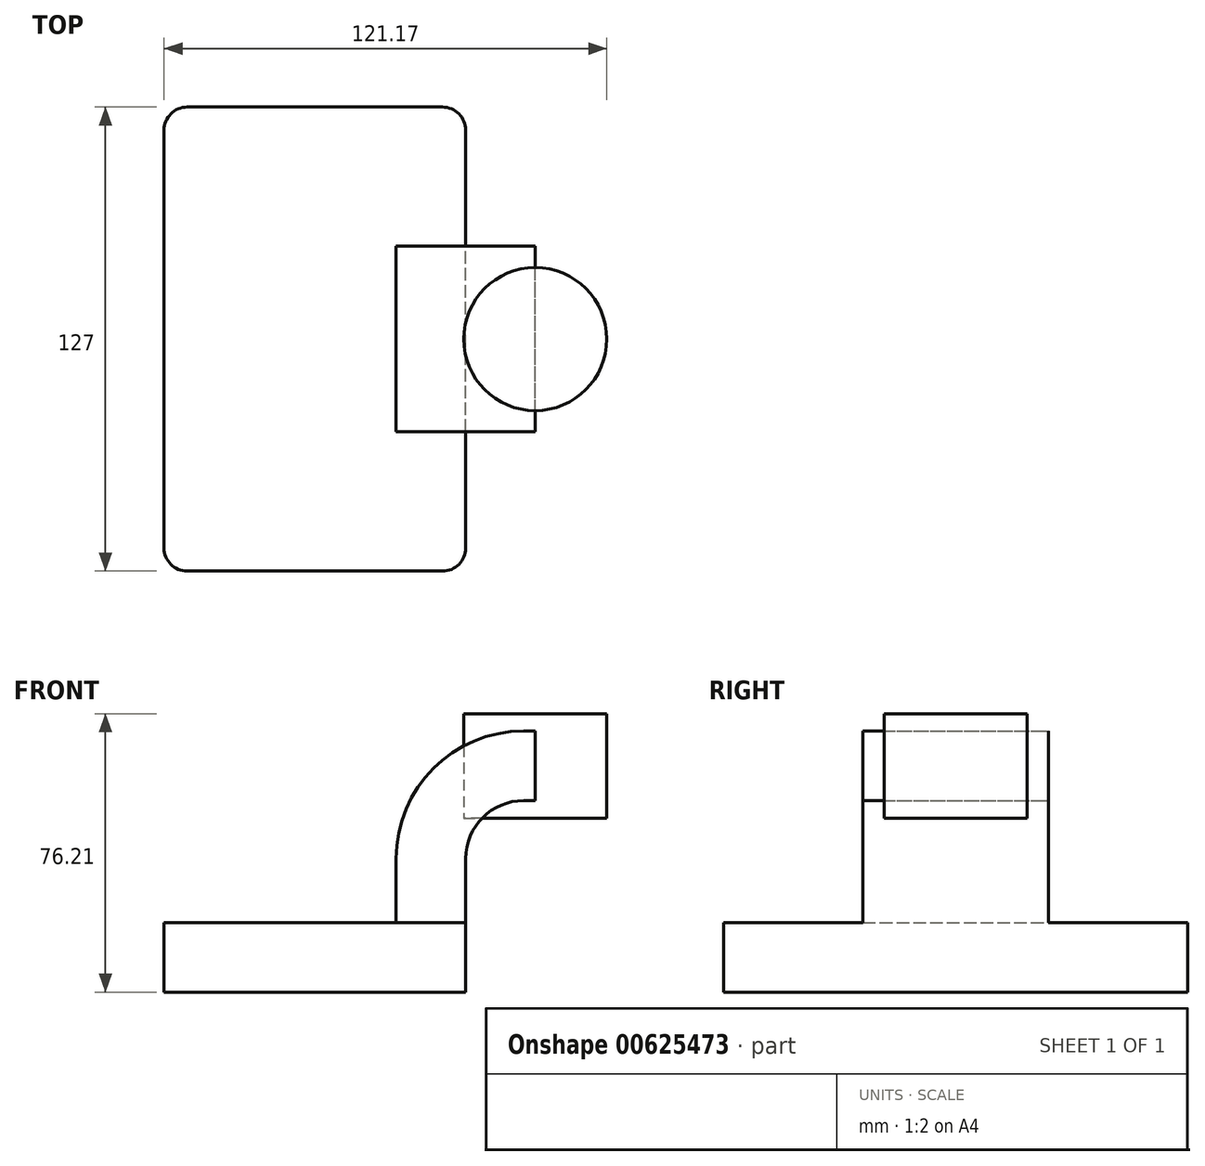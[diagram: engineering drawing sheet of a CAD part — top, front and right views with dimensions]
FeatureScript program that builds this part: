
annotation { "Feature Type Name" : "Feature", "Feature Type Description" : "" }
export const myFeature = defineFeature(function(context is Context, id is Id, definition is map)
    precondition{}
    {
        {
            var Q0;
            Q0=qCreatedBy(makeId("Front.planeOp"),FACE);
            var sketch = newSketch(context, id + "F0", { "sketchPlane" : qUnion([Q0])});
            skLineSegment(sketch, "E0.bottom", {"start": v(41.28, -9.52) * mm, "end": v(-41.28, -9.53) * mm});
            skLineSegment(sketch, "E0.top", {"start": v(41.28, 9.53) * mm, "end": v(-41.28, 9.53) * mm});
            skLineSegment(sketch, "E0.left", {"start": v(41.28, -9.52) * mm, "end": v(41.28, 9.53) * mm});
            skLineSegment(sketch, "E0.right", {"start": v(-41.28, -9.53) * mm, "end": v(-41.28, 9.53) * mm});
            skPoint(sketch, "E0.middle", {"position": v(0, 0) * mm});
            skLineSegment(sketch, "E1.bottom", {"start": v(60.32, 38.1) * mm, "end": v(111.12, 38.1) * mm});
            skLineSegment(sketch, "E1.top", {"start": v(60.32, 66.68) * mm, "end": v(111.12, 66.68) * mm});
            skLineSegment(sketch, "E1.left", {"start": v(60.32, 38.1) * mm, "end": v(60.32, 66.68) * mm});
            skLineSegment(sketch, "E1.right", {"start": v(111.12, 38.1) * mm, "end": v(111.12, 66.68) * mm});
            skPoint(sketch, "E1.middle", {"position": v(85.72, 52.39) * mm});
            skLineSegment(sketch, "E2", {"start": v(41.28, 9.53) * mm, "end": v(41.28, 27) * mm});
            skArc(sketch, "E3", {"start": v(41.28, 27) * mm, "mid": v(45.92, 38.23) * mm, "end": v(57.15, 42.88) * mm});
            skLineSegment(sketch, "E4", {"start": v(57.15, 42.88) * mm, "end": v(79.9, 42.88) * mm});
            skLineSegment(sketch, "E5.0", {"start": v(57.15, 61.93) * mm, "end": v(79.9, 61.93) * mm});
            skArc(sketch, "E5.1", {"start": v(22.23, 27) * mm, "mid": v(32.45, 51.7) * mm, "end": v(57.15, 61.93) * mm});
            skLineSegment(sketch, "E5.2", {"start": v(22.22, 9.53) * mm, "end": v(22.22, 27) * mm});
            skLineSegment(sketch, "E6", {"start": v(79.9, 38.1) * mm, "end": v(79.9, 66.68) * mm});
            skFitSpline(sketch, "E7", {"points": [v(-41.28, 9.52) * mm, v(57.15, 61.93) * mm], "startDerivative": vector(2.29, 73.75) * mm, "endDerivative": vector(146.95, -11.66) * mm});
            skSolve(sketch);
        }
        {
            var Q0;
            Q0=makeQuery(id+"F0.imprint","IMPRINT",FACE,{"disambiguationData":[TD([[makeQuery(id+"F0.imprint","IMPRINT",EDGE,{"derivedFrom":sQuery(id+"F0.wireOp",EDGE,"E0.bottom")}),-1.0]])]});
            extrude(context, id + "F1", {"entities" : qUnion([Q0]), "endBound" : BoundingType.SYMMETRIC, "depth" : 127 * mm, "offsetDistance" : 25.4 * mm});
        }
        {
            var Q0;
            {var subQ1=sQuery(id+"F0.wireOp",EDGE,"E2");Q0=makeQuery(id+"F0.imprint","IMPRINT",FACE,{"disambiguationData":[TD([[makeQuery(id+"F0.imprint","IMPRINT",EDGE,{"derivedFrom":subQ1}),1.0]])]});}
            extrude(context, id + "F2", {"entities" : qUnion([Q0]), "operationType" : NewBodyOperationType.ADD, "endBound" : BoundingType.SYMMETRIC, "depth" : 50.8 * mm, "offsetDistance" : 25.4 * mm});
        }
        {
            var Q0;
            Q0=makeQuery(id+"F0.imprint","IMPRINT",FACE,{"disambiguationData":[TD([[makeQuery(id+"F0.imprint","IMPRINT",EDGE,{"derivedFrom":sQuery(id+"F0.wireOp",EDGE,"E5.1")}),1.0]])]});
            extrude(context, id + "F3", {"entities" : qUnion([Q0]), "operationType" : NewBodyOperationType.ADD, "endBound" : BoundingType.SYMMETRIC, "depth" : 15.88 * mm, "offsetDistance" : 25.4 * mm});
        }
        {
            var Q0;
            {var subQ0=sQuery(id+"F0.wireOp",EDGE,"E4");var subQ1=sQuery(id+"F0.wireOp",EDGE,"E1.left");var subQ2=makeQuery(id+"F0.imprint","INTERSECT",VERTEX,{"derivedFrom":[subQ1,subQ0]});Q0=makeQuery(id+"F0.imprint","IMPRINT",FACE,{"disambiguationData":[TD([[makeQuery(id+"F0.imprint","IMPRINT",EDGE,{"disambiguationData":[TD([[subQ2,-1.0]])],"derivedFrom":subQ1}),-1.0]])]});}
            var Q1;
            {var subQ0=sQuery(id+"F0.wireOp",EDGE,"E1.left");var subQ1=sQuery(id+"F0.wireOp",EDGE,"E1.bottom");var subQ2=makeQuery(id+"F0.imprint","INTERSECT",VERTEX,{"derivedFrom":[subQ1,subQ0]});Q1=makeQuery(id+"F0.imprint","IMPRINT",FACE,{"disambiguationData":[TD([[makeQuery(id+"F0.imprint","IMPRINT",EDGE,{"disambiguationData":[TD([[subQ2,-1.0]])],"derivedFrom":subQ1}),1.0]])]});}
            var Q2;
            {var subQ0=sQuery(id+"F0.wireOp",EDGE,"E1.left");var subQ1=sQuery(id+"F0.wireOp",EDGE,"E1.top");var subQ2=makeQuery(id+"F0.imprint","INTERSECT",VERTEX,{"derivedFrom":[subQ1,subQ0]});Q2=makeQuery(id+"F0.imprint","IMPRINT",FACE,{"disambiguationData":[TD([[makeQuery(id+"F0.imprint","IMPRINT",EDGE,{"disambiguationData":[TD([[subQ2,-1.0]])],"derivedFrom":subQ1}),-1.0]])]});}
            var Q3;
            Q3=sQuery(id+"F0.wireOp",EDGE,"E1.left");
            revolve(context, id + "F4", {"entities" : qUnion([Q0, Q1, Q2]), "axis" : qUnion([Q3]), "revolveType" : RevolveType.FULL});
        }
        {
            var Q0;
            Q0=makeQuery(id+"F1.opExtrude","CAP_EDGE",EDGE,{"disambiguationData":[OSD([sQuery(id+"F0.wireOp",EDGE,"E0.left")])],"isStart":false});
            var Q1;
            Q1=makeQuery(id+"F1.opExtrude","CAP_EDGE",EDGE,{"disambiguationData":[OSD([sQuery(id+"F0.wireOp",EDGE,"E0.left")])],"isStart":true});
            var Q2;
            Q2=makeQuery(id+"F1.opExtrude","CAP_EDGE",EDGE,{"disambiguationData":[OSD([sQuery(id+"F0.wireOp",EDGE,"E0.right")])],"isStart":true});
            var Q3;
            Q3=makeQuery(id+"F1.opExtrude","CAP_EDGE",EDGE,{"disambiguationData":[OSD([sQuery(id+"F0.wireOp",EDGE,"E0.right")])],"isStart":false});
            fillet(context, id + "F5", {"entities" : qUnion([Q0, Q1, Q2, Q3]), "radius" : 6.35 * mm, "tangentPropagation" : true, "allowEdgeOverflow" : false});
        }
    });
